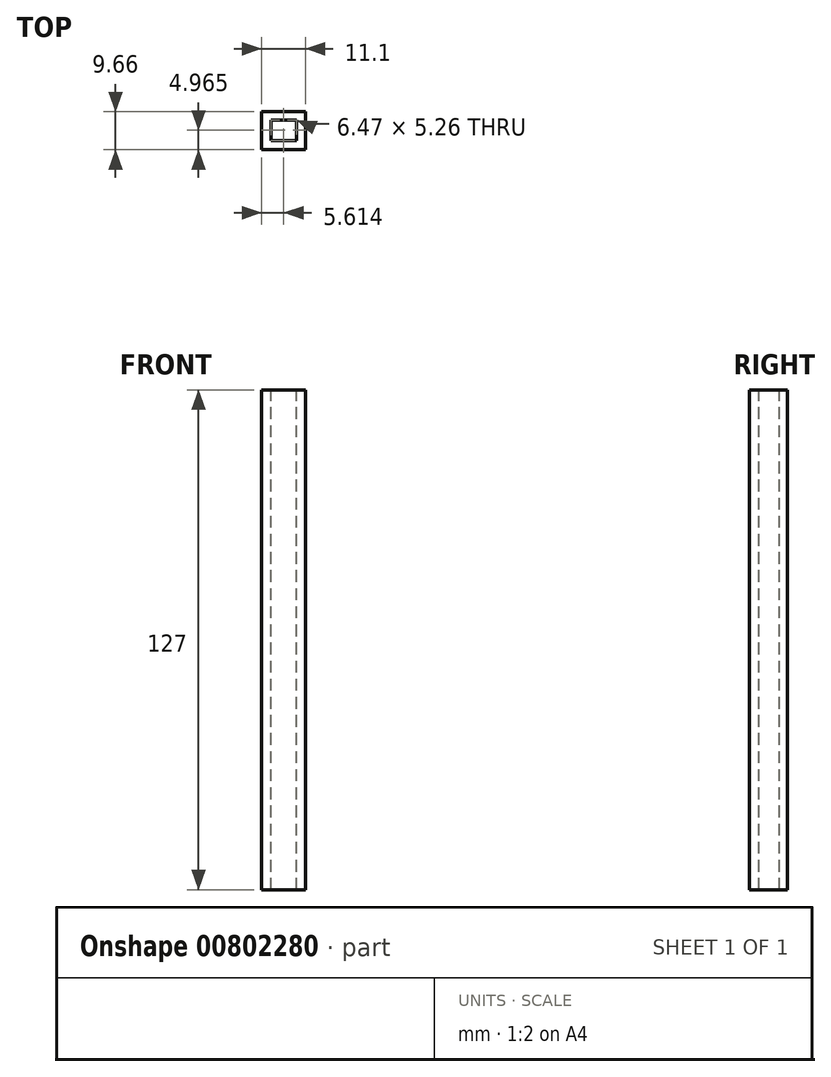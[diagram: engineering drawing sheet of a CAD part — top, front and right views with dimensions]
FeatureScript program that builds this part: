
annotation { "Feature Type Name" : "Feature", "Feature Type Description" : "" }
export const myFeature = defineFeature(function(context is Context, id is Id, definition is map)
    precondition{}
    {
        {
            var Q0;
            Q0=qCreatedBy(makeId("Top.planeOp"),FACE);
            var sketch = newSketch(context, id + "F0", { "sketchPlane" : qUnion([Q0])});
            skLineSegment(sketch, "E0.bottom", {"start": v(0, 0) * mm, "end": v(11.1, 0) * mm});
            skLineSegment(sketch, "E0.top", {"start": v(0, 9.66) * mm, "end": v(11.1, 9.66) * mm});
            skLineSegment(sketch, "E0.left", {"start": v(0, 0) * mm, "end": v(0, 9.66) * mm});
            skLineSegment(sketch, "E0.right", {"start": v(11.1, 0) * mm, "end": v(11.1, 9.66) * mm});
            skSolve(sketch);
        }
        {
            var Q0;
            Q0 = qSketchRegion(id + "F0", true);
            extrude(context, id + "F1", {"entities" : qUnion([Q0]), "depth" : 127 * mm, "offsetDistance" : 25.4 * mm});
        }
        {
            var Q0;
            Q0=makeQuery(id+"F1.opExtrude","CAP_FACE",FACE,{"disambiguationData":[OSD([sQuery(id+"F0.wireOp",EDGE,"E0.bottom"),sQuery(id+"F0.wireOp",EDGE,"E0.top"),sQuery(id+"F0.wireOp",EDGE,"E0.left"),sQuery(id+"F0.wireOp",EDGE,"E0.right")])],"isStart":false});
            var sketch = newSketch(context, id + "F2", { "sketchPlane" : qUnion([Q0])});
            skLineSegment(sketch, "E1.bottom", {"start": v(2.38, 2.34) * mm, "end": v(8.85, 2.34) * mm});
            skLineSegment(sketch, "E1.top", {"start": v(2.38, 7.6) * mm, "end": v(8.85, 7.6) * mm});
            skLineSegment(sketch, "E1.left", {"start": v(2.38, 2.34) * mm, "end": v(2.38, 7.6) * mm});
            skLineSegment(sketch, "E1.right", {"start": v(8.85, 2.34) * mm, "end": v(8.85, 7.6) * mm});
            skSolve(sketch);
        }
        {
            var Q0;
            Q0 = qSketchRegion(id + "F2", true);
            extrude(context, id + "F3", {"entities" : qUnion([Q0]), "operationType" : NewBodyOperationType.REMOVE, "oppositeDirection" : true, "depth" : 127.2 * mm, "offsetDistance" : 25 * mm, "hasSecondDirection" : true, "secondDirectionOppositeDirection" : false, "secondDirectionDepth" : 25 * mm});
        }
    });
